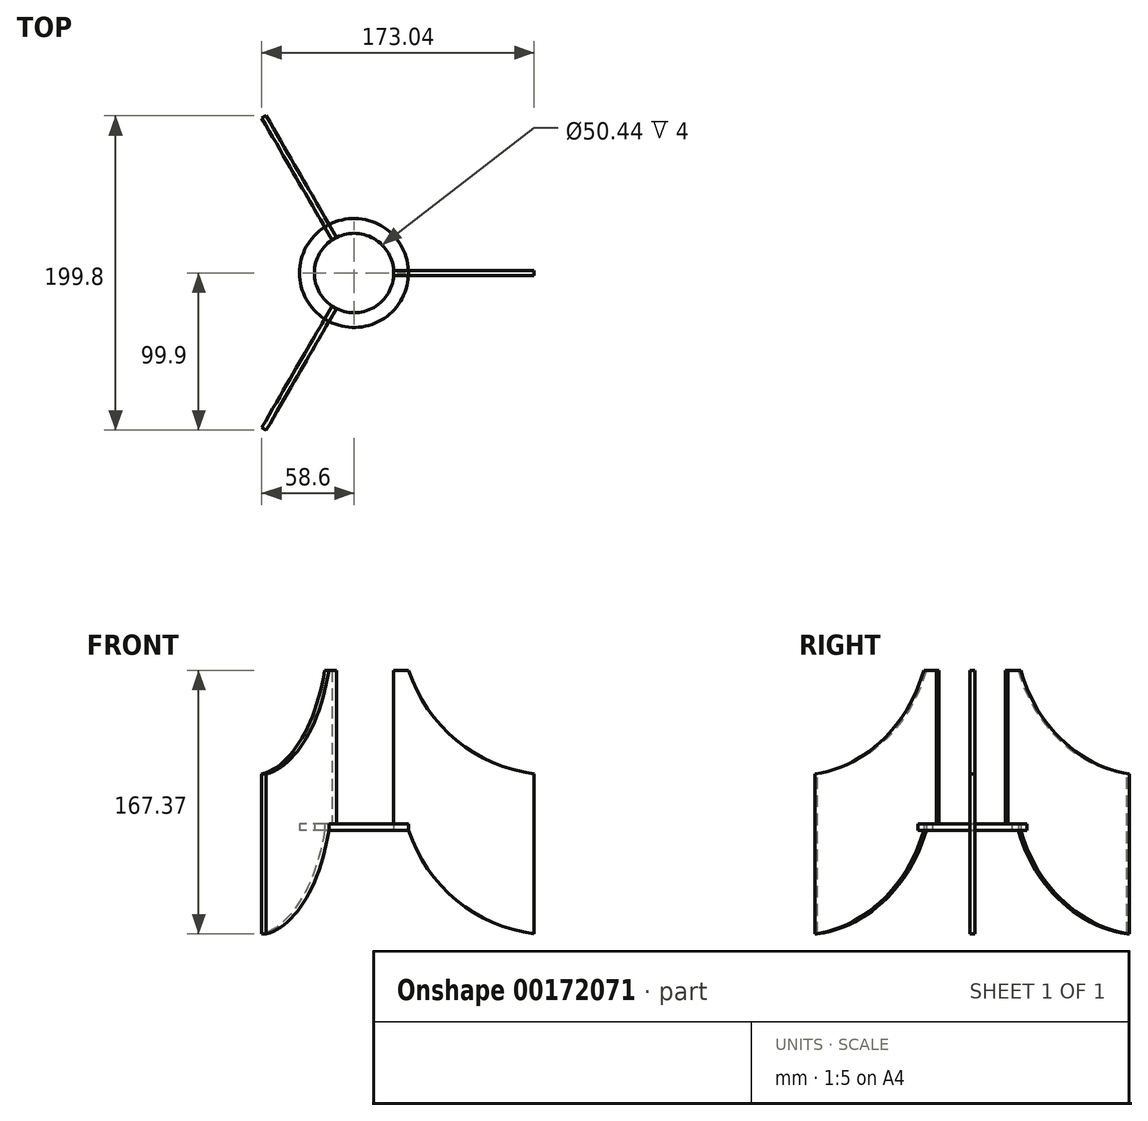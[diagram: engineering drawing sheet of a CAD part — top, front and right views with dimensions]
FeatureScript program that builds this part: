
annotation { "Feature Type Name" : "Feature", "Feature Type Description" : "" }
export const myFeature = defineFeature(function(context is Context, id is Id, definition is map)
    precondition{}
    {
        {
            assignVariable(context, id + "F0", {"name" : "TubeHeight", "anyValue" : 4});
        }
        {
            var Q0;
            Q0=qCreatedBy(makeId("Top.planeOp"),FACE);
            var sketch = newSketch(context, id + "F1", { "sketchPlane" : qUnion([Q0])});
            skCircle(sketch, "E0", {"center": v(0, 0) * mm, "radius": 34.62 * mm});
            skCircle(sketch, "E1", {"center": v(0, 0) * mm, "radius": 25.22 * mm});
            skSolve(sketch);
        }
        {
            var Q0;
            Q0 = qSketchRegion(id + "F1", true);
            extrude(context, id + "F2", {"entities" : qUnion([Q0]), "depth" : (getVariable(context, 'TubeHeight')) * mm});
        }
        {
            var Q0;
            Q0=qCreatedBy(makeId("Front.planeOp"),FACE);
            var sketch = newSketch(context, id + "F3", { "sketchPlane" : qUnion([Q0])});
            skLineSegment(sketch, "E2.0", {"start": v(-34.62, 101.6) * mm, "end": v(34.62, 101.6) * mm, "construction": true});
            skLineSegment(sketch, "E3.0", {"start": v(-34.62, 0) * mm, "end": v(34.62, 0) * mm, "construction": true});
            skLineSegment(sketch, "E4", {"start": v(34.62, 101.6) * mm, "end": v(34.62, 0) * mm});
            skArc(sketch, "E5", {"start": v(34.62, 0) * mm, "mid": v(65.02, -44.42) * mm, "end": v(114.44, -65.77) * mm});
            skLineSegment(sketch, "E6", {"start": v(114.44, -65.77) * mm, "end": v(114.44, 35.83) * mm});
            skArc(sketch, "E7.0.1.0", {"start": v(34.62, 101.6) * mm, "mid": v(65.02, 57.18) * mm, "end": v(114.44, 35.83) * mm});
            skLineSegment(sketch, "E7.direction1", {"start": v(34.62, 0) * mm, "end": v(60.02, 0) * mm, "construction": true});
            skLineSegment(sketch, "E7.direction2", {"start": v(34.62, 0) * mm, "end": v(34.62, 101.6) * mm, "construction": true});
            skLineSegment(sketch, "E8.0", {"start": v(-25.22, 101.6) * mm, "end": v(25.22, 101.6) * mm});
            skLineSegment(sketch, "E9.0", {"start": v(-25.22, 0) * mm, "end": v(25.22, 0) * mm});
            skLineSegment(sketch, "E10", {"start": v(25.22, 101.6) * mm, "end": v(25.22, 0) * mm});
            skLineSegment(sketch, "E11", {"start": v(25.22, 101.6) * mm, "end": v(34.62, 101.6) * mm});
            skLineSegment(sketch, "E12", {"start": v(25.22, 0) * mm, "end": v(34.62, 0) * mm});
            skSolve(sketch);
        }
        {
            var Q0;
            Q0=makeQuery(id+"F3.imprint","IMPRINT",FACE,{"disambiguationData":[TD([[makeQuery(id+"F3.imprint","IMPRINT",EDGE,{"derivedFrom":sQuery(id+"F3.wireOp",EDGE,"E4")}),1.0]])]});
            var Q1;
            Q1=makeQuery(id+"F3.imprint","IMPRINT",FACE,{"disambiguationData":[TD([[makeQuery(id+"F3.imprint","IMPRINT",EDGE,{"derivedFrom":sQuery(id+"F3.wireOp",EDGE,"E4")}),-1.0]])]});
            extrude(context, id + "F4", {"entities" : qUnion([Q0, Q1]), "depth" : 1.59 * mm, "hasSecondDirection" : true, "secondDirectionOppositeDirection" : true, "secondDirectionDepth" : 1.59 * mm});
        }
        {
            var Q0;
            Q0=makeQuery(id+"F4.opExtrude","SWEPT_BODY",BODY,{"disambiguationData":[OSD([sQuery(id+"F3.wireOp",EDGE,"E5"),sQuery(id+"F3.wireOp",EDGE,"E6"),sQuery(id+"F3.wireOp",EDGE,"E7.0.1.0"),sQuery(id+"F3.wireOp",EDGE,"E10"),sQuery(id+"F3.wireOp",EDGE,"E11"),sQuery(id+"F3.wireOp",EDGE,"E12")])]});
            var Q1;
            Q1=makeQuery(id+"F2.opExtrude","SWEPT_FACE",FACE,{"disambiguationData":[OSD([sQuery(id+"F1.wireOp",EDGE,"E0")])]});
            circularPattern(context, id + "F5", {"operationType" : NewBodyOperationType.ADD, "entities" : qUnion([Q0]), "axis" : qUnion([Q1]), "angle" : 120 * degree, "instanceCount" : 3});
        }
    });
